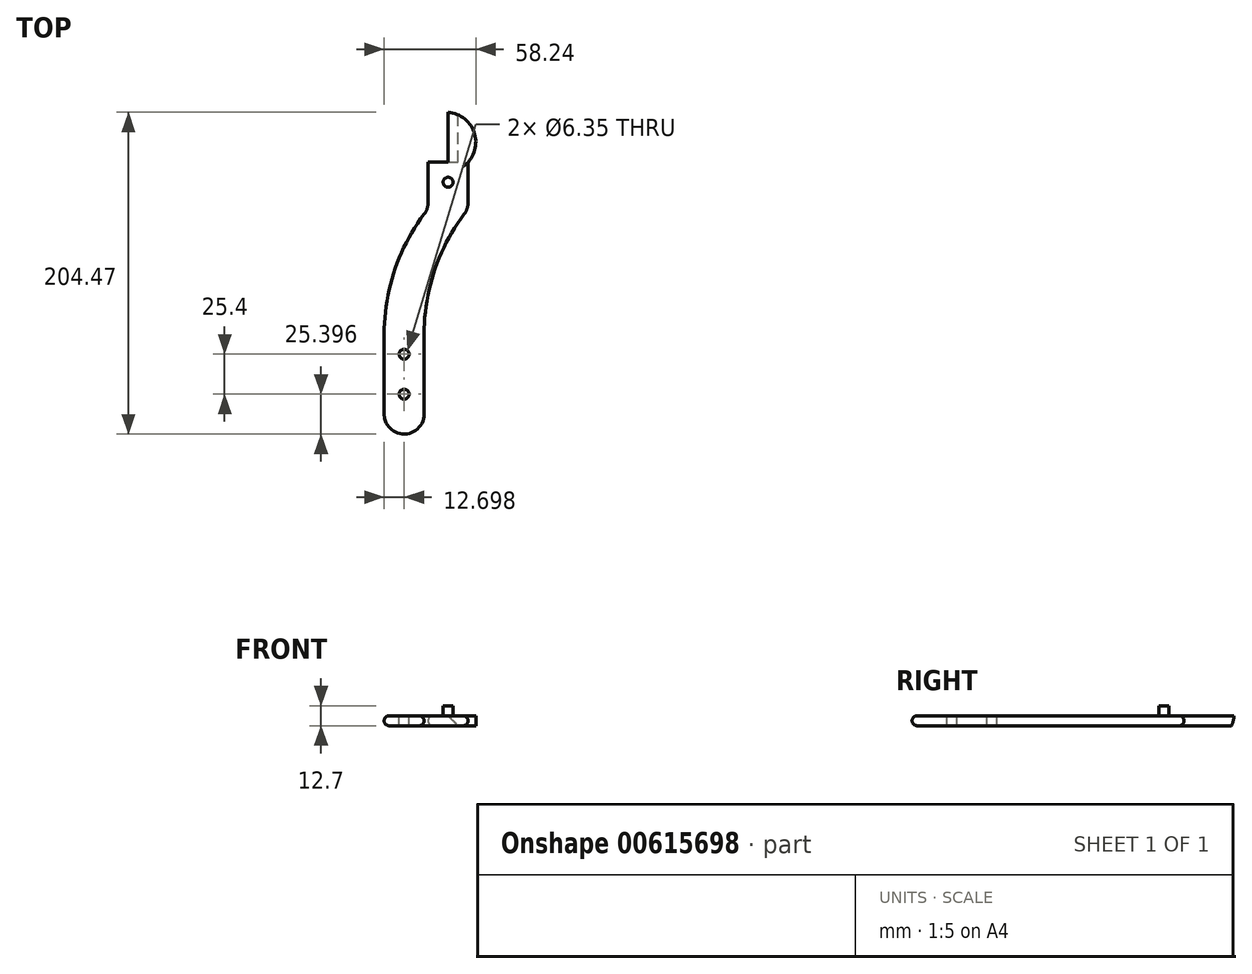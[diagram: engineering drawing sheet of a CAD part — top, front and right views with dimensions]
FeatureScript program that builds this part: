
annotation { "Feature Type Name" : "Feature", "Feature Type Description" : "" }
export const myFeature = defineFeature(function(context is Context, id is Id, definition is map)
    precondition{}
    {
        {
            var Q0;
            Q0=qCreatedBy(makeId("Top.planeOp"),FACE);
            var sketch = newSketch(context, id + "F0", { "sketchPlane" : qUnion([Q0])});
            skArc(sketch, "E0", {"start": v(-10.51, -79.24) * mm, "mid": v(2.19, -91.94) * mm, "end": v(14.89, -79.24) * mm});
            skLineSegment(sketch, "E1", {"start": v(-10.51, -79.24) * mm, "end": v(-10.51, -28.44) * mm});
            skLineSegment(sketch, "E2", {"start": v(14.89, -79.24) * mm, "end": v(14.89, -28.44) * mm});
            skArc(sketch, "E3", {"start": v(40.29, 47.76) * mm, "mid": v(21.4, 11.72) * mm, "end": v(14.89, -28.44) * mm});
            skArc(sketch, "E4", {"start": v(14.89, 47.76) * mm, "mid": v(-4, 11.72) * mm, "end": v(-10.51, -28.44) * mm});
            skLineSegment(sketch, "E5", {"start": v(42.83, 55.38) * mm, "end": v(42.83, 80.78) * mm});
            skLineSegment(sketch, "E6", {"start": v(17.43, 55.38) * mm, "end": v(17.43, 80.78) * mm});
            skPoint(sketch, "E7.visualSharp", {"position": v(42.83, 51.03) * mm});
            skArc(sketch, "E7.filletArc", {"start": v(40.29, 47.76) * mm, "mid": v(42.18, 51.36) * mm, "end": v(42.83, 55.38) * mm});
            skPoint(sketch, "E8.visualSharp", {"position": v(17.43, 51.03) * mm});
            skArc(sketch, "E8.filletArc", {"start": v(14.89, 47.76) * mm, "mid": v(16.78, 51.36) * mm, "end": v(17.43, 55.38) * mm});
            skLineSegment(sketch, "E9", {"start": v(17.43, 80.78) * mm, "end": v(30.13, 80.78) * mm});
            skLineSegment(sketch, "E10", {"start": v(30.13, 80.78) * mm, "end": v(30.13, 112.53) * mm});
            skArc(sketch, "E11", {"start": v(42.83, 80.78) * mm, "mid": v(46.37, 100.6) * mm, "end": v(30.13, 112.53) * mm});
            skSolve(sketch);
        }
        {
            var Q0;
            Q0 = qSketchRegion(id + "F0", true);
            extrude(context, id + "F1", {"entities" : qUnion([Q0]), "depth" : 6.35 * mm, "offsetDistance" : 25.4 * mm});
        }
        {
            var Q0;
            Q0=makeQuery(id+"F1.opExtrude","CAP_EDGE",EDGE,{"disambiguationData":[OSD([sQuery(id+"F0.wireOp",EDGE,"E10")])],"isStart":true});
            chamfer(context, id + "F2", {"entities" : qUnion([Q0]), "width" : 6.35 * mm, "tangentPropagation" : true});
        }
        {
            var Q0;
            Q0=makeQuery(id+"F1.opExtrude","CAP_FACE",FACE,{"disambiguationData":[OSD([sQuery(id+"F0.wireOp",EDGE,"E0"),sQuery(id+"F0.wireOp",EDGE,"E1"),sQuery(id+"F0.wireOp",EDGE,"E2"),sQuery(id+"F0.wireOp",EDGE,"E3"),sQuery(id+"F0.wireOp",EDGE,"E4"),sQuery(id+"F0.wireOp",EDGE,"E5"),sQuery(id+"F0.wireOp",EDGE,"E6"),sQuery(id+"F0.wireOp",EDGE,"E7.filletArc"),sQuery(id+"F0.wireOp",EDGE,"E8.filletArc"),sQuery(id+"F0.wireOp",EDGE,"E9"),sQuery(id+"F0.wireOp",EDGE,"E10"),sQuery(id+"F0.wireOp",EDGE,"E11")])],"isStart":false});
            var sketch = newSketch(context, id + "F3", { "sketchPlane" : qUnion([Q0])});
            skCircle(sketch, "E12", {"center": v(30.13, 68.08) * mm, "radius": 3.18 * mm});
            skSolve(sketch);
        }
        {
            var Q0;
            Q0 = qSketchRegion(id + "F3", true);
            extrude(context, id + "F4", {"entities" : qUnion([Q0]), "operationType" : NewBodyOperationType.ADD, "depth" : 6.35 * mm, "offsetDistance" : 25.4 * mm});
        }
        {
            var Q0;
            Q0=makeQuery(id+"F1.opExtrude","CAP_EDGE",EDGE,{"disambiguationData":[OSD([sQuery(id+"F0.wireOp",EDGE,"E8.filletArc")])],"isStart":false});
            var Q1;
            Q1=makeQuery(id+"F1.opExtrude","CAP_EDGE",EDGE,{"disambiguationData":[OSD([sQuery(id+"F0.wireOp",EDGE,"E4")])],"isStart":true});
            fillet(context, id + "F5", {"entities" : qUnion([Q0, Q1]), "radius" : 3.17 * mm, "tangentPropagation" : true, "allowEdgeOverflow" : false});
        }
        {
            var Q0;
            Q0=makeQuery(id+"F1.opExtrude","CAP_FACE",FACE,{"disambiguationData":[OSD([sQuery(id+"F0.wireOp",EDGE,"E0"),sQuery(id+"F0.wireOp",EDGE,"E1"),sQuery(id+"F0.wireOp",EDGE,"E2"),sQuery(id+"F0.wireOp",EDGE,"E3"),sQuery(id+"F0.wireOp",EDGE,"E4"),sQuery(id+"F0.wireOp",EDGE,"E5"),sQuery(id+"F0.wireOp",EDGE,"E6"),sQuery(id+"F0.wireOp",EDGE,"E7.filletArc"),sQuery(id+"F0.wireOp",EDGE,"E8.filletArc"),sQuery(id+"F0.wireOp",EDGE,"E9"),sQuery(id+"F0.wireOp",EDGE,"E10"),sQuery(id+"F0.wireOp",EDGE,"E11")])],"isStart":false});
            var sketch = newSketch(context, id + "F6", { "sketchPlane" : qUnion([Q0])});
            skCircle(sketch, "E13", {"center": v(2.19, -41.14) * mm, "radius": 3.18 * mm});
            skCircle(sketch, "E14", {"center": v(2.19, -66.54) * mm, "radius": 3.18 * mm});
            skSolve(sketch);
        }
        {
            var Q0;
            Q0 = qSketchRegion(id + "F6", true);
            extrude(context, id + "F7", {"entities" : qUnion([Q0]), "operationType" : NewBodyOperationType.REMOVE, "oppositeDirection" : true, "depth" : 6.35 * mm, "offsetDistance" : 25.4 * mm});
        }
    });
